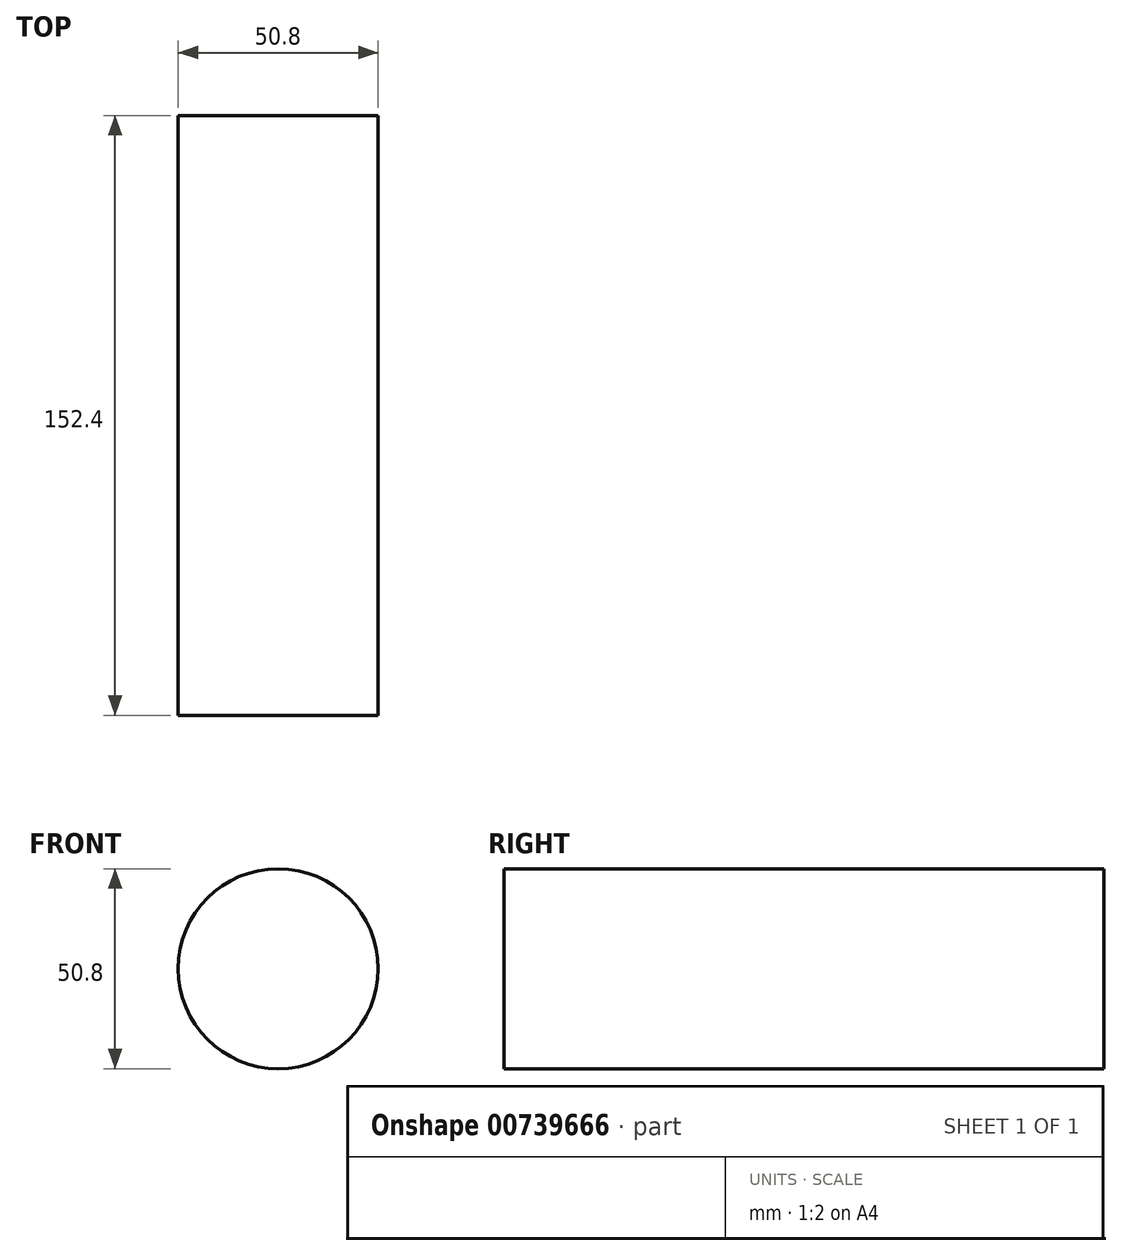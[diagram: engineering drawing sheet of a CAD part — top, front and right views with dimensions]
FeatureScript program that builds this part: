
annotation { "Feature Type Name" : "Feature", "Feature Type Description" : "" }
export const myFeature = defineFeature(function(context is Context, id is Id, definition is map)
    precondition{}
    {
        {
            var Q0;
            Q0=qCreatedBy(makeId("Front.planeOp"),FACE);
            var sketch = newSketch(context, id + "F0", { "sketchPlane" : qUnion([Q0])});
            skCircle(sketch, "E0", {"center": v(0, 0) * mm, "radius": 25.4 * mm});
            skSolve(sketch);
        }
        {
            var Q0;
            Q0 = qSketchRegion(id + "F0", true);
            extrude(context, id + "F1", {"entities" : qUnion([Q0]), "depth" : 152.4 * mm, "offsetDistance" : 25.4 * mm});
        }
    });
